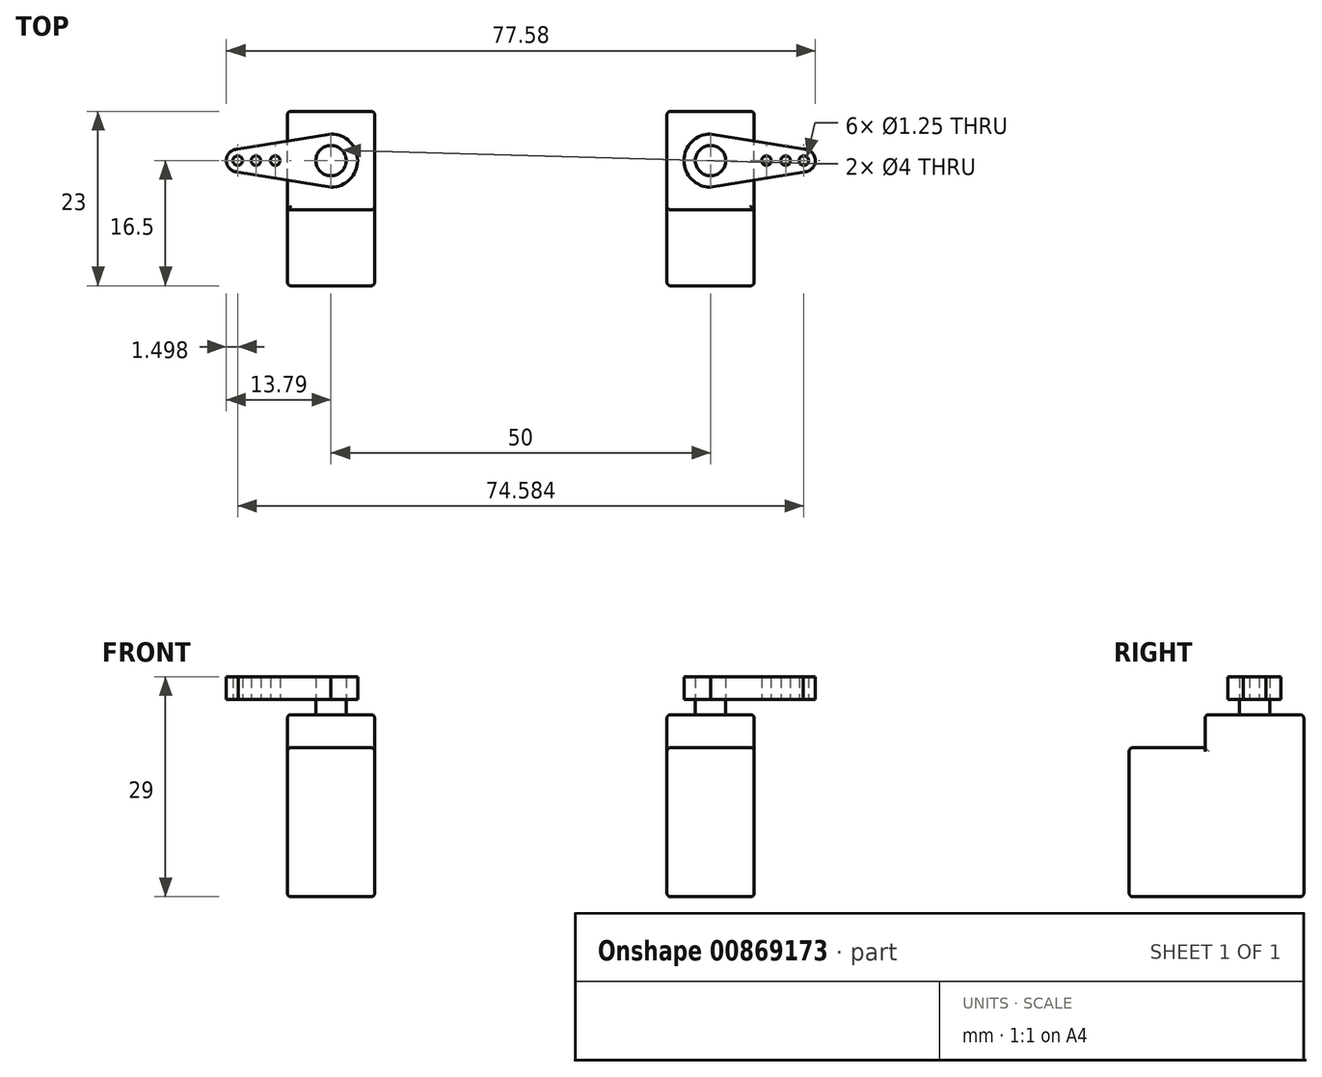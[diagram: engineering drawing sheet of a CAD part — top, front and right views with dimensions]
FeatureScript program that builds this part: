
annotation { "Feature Type Name" : "Feature", "Feature Type Description" : "" }
export const myFeature = defineFeature(function(context is Context, id is Id, definition is map)
    precondition{}
    {
        {
            var Q0;
            Q0=qCreatedBy(makeId("Top.planeOp"),FACE);
            var sketch = newSketch(context, id + "F0", { "sketchPlane" : qUnion([Q0])});
            skLineSegment(sketch, "E0.bottom", {"start": v(5.75, -11.5) * mm, "end": v(-5.75, -11.5) * mm});
            skLineSegment(sketch, "E0.top", {"start": v(5.75, 11.5) * mm, "end": v(-5.75, 11.5) * mm});
            skLineSegment(sketch, "E0.left", {"start": v(5.75, -11.5) * mm, "end": v(5.75, 11.5) * mm});
            skLineSegment(sketch, "E0.right", {"start": v(-5.75, -11.5) * mm, "end": v(-5.75, 11.5) * mm});
            skPoint(sketch, "E0.middle", {"position": v(0, 0) * mm});
            skSolve(sketch);
        }
        {
            var Q0;
            Q0 = qSketchRegion(id + "F0", true);
            extrude(context, id + "F1", {"entities" : qUnion([Q0]), "depth" : 19.65 * mm, "offsetDistance" : 25 * mm});
        }
        {
            var Q0;
            Q0=makeQuery(id+"F1.opExtrude","CAP_FACE",FACE,{"disambiguationData":[OSD([sQuery(id+"F0.wireOp",EDGE,"E0.bottom"),sQuery(id+"F0.wireOp",EDGE,"E0.top"),sQuery(id+"F0.wireOp",EDGE,"E0.left"),sQuery(id+"F0.wireOp",EDGE,"E0.right")])],"isStart":false});
            var sketch = newSketch(context, id + "F2", { "sketchPlane" : qUnion([Q0])});
            skLineSegment(sketch, "E1.bottom", {"start": v(-5.75, 11.5) * mm, "end": v(5.75, 11.5) * mm});
            skLineSegment(sketch, "E1.top", {"start": v(-5.75, -1.5) * mm, "end": v(5.75, -1.5) * mm});
            skLineSegment(sketch, "E1.left", {"start": v(-5.75, 11.5) * mm, "end": v(-5.75, -1.5) * mm});
            skLineSegment(sketch, "E1.right", {"start": v(5.75, 11.5) * mm, "end": v(5.75, -1.5) * mm});
            skSolve(sketch);
        }
        {
            var Q0;
            Q0=makeQuery(id+"F2.imprint","IMPRINT",FACE,{"disambiguationData":[TD([[makeQuery(id+"F2.imprint","IMPRINT",EDGE,{"derivedFrom":sQuery(id+"F2.wireOp",EDGE,"E1.bottom")}),1.0]])]});
            extrude(context, id + "F3", {"entities" : qUnion([Q0]), "operationType" : NewBodyOperationType.ADD, "depth" : 4.35 * mm, "offsetDistance" : 25 * mm});
        }
        {
            var Q0;
            Q0=makeQuery(id+"F1.opExtrude","SWEPT_EDGE",EDGE,{"disambiguationData":[OSD([sQuery(id+"F0.wireOp",EDGE,"E0.bottom"),sQuery(id+"F0.wireOp",EDGE,"E0.right")])]});
            var Q1;
            Q1=makeQuery(id+"F1.opExtrude","SWEPT_EDGE",EDGE,{"disambiguationData":[OSD([sQuery(id+"F0.wireOp",EDGE,"E0.bottom"),sQuery(id+"F0.wireOp",EDGE,"E0.left")])]});
            var Q2;
            Q2=makeQuery(id+"F3.boolean.opBoolean","MERGE",EDGE,{"derivedFrom":[makeQuery(id+"F1.opExtrude","SWEPT_EDGE",EDGE,{"disambiguationData":[OSD([sQuery(id+"F0.wireOp",EDGE,"E0.top"),sQuery(id+"F0.wireOp",EDGE,"E0.right")])]}),makeQuery(id+"F3.opExtrude","SWEPT_EDGE",EDGE,{"disambiguationData":[OSD([sQuery(id+"F2.wireOp",EDGE,"E1.bottom"),sQuery(id+"F2.wireOp",EDGE,"E1.left")])]})]});
            var Q3;
            Q3=makeQuery(id+"F3.boolean.opBoolean","MERGE",EDGE,{"derivedFrom":[makeQuery(id+"F1.opExtrude","SWEPT_EDGE",EDGE,{"disambiguationData":[OSD([sQuery(id+"F0.wireOp",EDGE,"E0.top"),sQuery(id+"F0.wireOp",EDGE,"E0.left")])]}),makeQuery(id+"F3.opExtrude","SWEPT_EDGE",EDGE,{"disambiguationData":[OSD([sQuery(id+"F2.wireOp",EDGE,"E1.bottom"),sQuery(id+"F2.wireOp",EDGE,"E1.right")])]})]});
            var Q4;
            Q4=makeQuery(id+"F1.opExtrude","CAP_EDGE",EDGE,{"disambiguationData":[OSD([sQuery(id+"F0.wireOp",EDGE,"E0.left")])],"isStart":true});
            var Q5;
            Q5=makeQuery(id+"F1.opExtrude","CAP_EDGE",EDGE,{"disambiguationData":[OSD([sQuery(id+"F0.wireOp",EDGE,"E0.right")])],"isStart":true});
            var Q6;
            Q6=makeQuery(id+"F1.opExtrude","CAP_EDGE",EDGE,{"disambiguationData":[OSD([sQuery(id+"F0.wireOp",EDGE,"E0.bottom")])],"isStart":false});
            var Q7;
            Q7=makeQuery(id+"F1.opExtrude","CAP_EDGE",EDGE,{"disambiguationData":[OSD([sQuery(id+"F0.wireOp",EDGE,"E0.right")])],"isStart":false});
            var Q8;
            Q8=makeQuery(id+"F3.opExtrude","SWEPT_EDGE",EDGE,{"disambiguationData":[OSD([sQuery(id+"F0.wireOp",EDGE,"E0.right"),sQuery(id+"F2.wireOp",EDGE,"E1.top"),sQuery(id+"F2.wireOp",EDGE,"E1.left")])]});
            var Q9;
            Q9=makeQuery(id+"F3.opExtrude","CAP_EDGE",EDGE,{"disambiguationData":[OSD([sQuery(id+"F2.wireOp",EDGE,"E1.left")])],"isStart":false});
            var Q10;
            Q10=makeQuery(id+"F3.opExtrude","CAP_EDGE",EDGE,{"disambiguationData":[OSD([sQuery(id+"F2.wireOp",EDGE,"E1.top")])],"isStart":false});
            var Q11;
            Q11=makeQuery(id+"F3.opExtrude","CAP_EDGE",EDGE,{"disambiguationData":[OSD([sQuery(id+"F2.wireOp",EDGE,"E1.right")])],"isStart":false});
            var Q12;
            Q12=makeQuery(id+"F1.opExtrude","CAP_EDGE",EDGE,{"disambiguationData":[OSD([sQuery(id+"F0.wireOp",EDGE,"E0.left")])],"isStart":false});
            var Q13;
            Q13=makeQuery(id+"F3.opExtrude","CAP_EDGE",EDGE,{"disambiguationData":[OSD([sQuery(id+"F2.wireOp",EDGE,"E1.bottom")])],"isStart":false});
            var Q14;
            Q14=makeQuery(id+"F1.opExtrude","CAP_EDGE",EDGE,{"disambiguationData":[OSD([sQuery(id+"F0.wireOp",EDGE,"E0.top")])],"isStart":true});
            var Q15;
            Q15=makeQuery(id+"F1.opExtrude","CAP_EDGE",EDGE,{"disambiguationData":[OSD([sQuery(id+"F0.wireOp",EDGE,"E0.bottom")])],"isStart":true});
            fillet(context, id + "F4", {"entities" : qUnion([Q0, Q1, Q2, Q3, Q4, Q5, Q6, Q7, Q8, Q9, Q10, Q11, Q12, Q13, Q14, Q15]), "radius" : .5 * mm, "tangentPropagation" : true, "allowEdgeOverflow" : false});
        }
        {
            var Q0;
            Q0=makeQuery(id+"F3.opExtrude","CAP_FACE",FACE,{"disambiguationData":[OSD([sQuery(id+"F2.wireOp",EDGE,"E1.bottom"),sQuery(id+"F2.wireOp",EDGE,"E1.top"),sQuery(id+"F2.wireOp",EDGE,"E1.left"),sQuery(id+"F2.wireOp",EDGE,"E1.right")])],"isStart":false});
            var sketch = newSketch(context, id + "F5", { "sketchPlane" : qUnion([Q0])});
            skCircle(sketch, "E2", {"center": v(0, 5) * mm, "radius": 2 * mm});
            skSolve(sketch);
        }
        {
            var Q0;
            Q0=makeQuery(id+"F5.imprint","IMPRINT",FACE,{"disambiguationData":[TD([[makeQuery(id+"F5.imprint","IMPRINT",EDGE,{"derivedFrom":sQuery(id+"F5.wireOp",EDGE,"E2")}),1.0]])]});
            extrude(context, id + "F6", {"entities" : qUnion([Q0]), "operationType" : NewBodyOperationType.ADD, "depth" : 5 * mm, "offsetDistance" : 25 * mm});
        }
        {
            var Q0;
            Q0=makeQuery(id+"F3.opExtrude","CAP_FACE",FACE,{"disambiguationData":[OSD([sQuery(id+"F2.wireOp",EDGE,"E1.bottom"),sQuery(id+"F2.wireOp",EDGE,"E1.top"),sQuery(id+"F2.wireOp",EDGE,"E1.left"),sQuery(id+"F2.wireOp",EDGE,"E1.right")])],"isStart":false});
            var sketch = newSketch(context, id + "F7", { "sketchPlane" : qUnion([Q0])});
            skCircle(sketch, "E3.0", {"center": v(0, 5) * mm, "radius": 2 * mm});
            skArc(sketch, "E4", {"start": v(0, 8.5) * mm, "mid": v(-3.5, 5) * mm, "end": v(0, 1.5) * mm});
            skArc(sketch, "E5", {"start": v(12.2, 3.5) * mm, "mid": v(13.8, 4.97) * mm, "end": v(12.26, 6.5) * mm});
            skLineSegment(sketch, "E6", {"start": v(0, 8.5) * mm, "end": v(12.26, 6.5) * mm});
            skLineSegment(sketch, "E7", {"start": v(0, 1.5) * mm, "end": v(12.2, 3.5) * mm});
            skCircle(sketch, "E8", {"center": v(12.3, 5) * mm, "radius": 0.62 * mm});
            skCircle(sketch, "E9", {"center": v(9.89, 5) * mm, "radius": 0.62 * mm});
            skCircle(sketch, "E10", {"center": v(7.35, 5) * mm, "radius": 0.62 * mm});
            skSolve(sketch);
        }
        {
            var Q0;
            Q0=makeQuery(id+"F7.imprint","IMPRINT",FACE,{"disambiguationData":[TD([[makeQuery(id+"F7.imprint","IMPRINT",EDGE,{"derivedFrom":sQuery(id+"F7.wireOp",EDGE,"E3.0")}),-1.0]])]});
            var Q1;
            {var subQ1=sQuery(id+"F7.wireOp",EDGE,"E5");Q1=makeQuery(id+"F7.imprint","IMPRINT",FACE,{"disambiguationData":[TD([[makeQuery(id+"F7.imprint","IMPRINT",EDGE,{"derivedFrom":subQ1}),1.0]])]});}
            extrude(context, id + "F8", {"entities" : qUnion([Q0, Q1]), "depth" : 3 * mm, "offsetDistance" : 25 * mm});
        }
        {
            var Q0;
            Q0=makeQuery(id+"F8.opExtrude","SWEPT_BODY",BODY,{"disambiguationData":[OSD([sQuery(id+"F7.wireOp",EDGE,"E3.0"),sQuery(id+"F7.wireOp",EDGE,"E4"),sQuery(id+"F7.wireOp",EDGE,"E5"),sQuery(id+"F7.wireOp",EDGE,"E6"),sQuery(id+"F7.wireOp",EDGE,"E7"),sQuery(id+"F7.wireOp",EDGE,"E8"),sQuery(id+"F7.wireOp",EDGE,"E9"),sQuery(id+"F7.wireOp",EDGE,"E10")])]});
            transform(context, id + "F9", {"entities" : qUnion([Q0]), "transformType" : TransformType.TRANSLATION_3D, "dx" : 0 * mm, "dy" : 0 * mm, "dz" : 2 * mm, "makeCopy" : false});
        }
        {
            var Q0;
            Q0=makeQuery(id+"F1.opExtrude","SWEPT_BODY",BODY,{"disambiguationData":[OSD([sQuery(id+"F0.wireOp",EDGE,"E0.bottom"),sQuery(id+"F0.wireOp",EDGE,"E0.top"),sQuery(id+"F0.wireOp",EDGE,"E0.left"),sQuery(id+"F0.wireOp",EDGE,"E0.right")])]});
            var Q1;
            Q1=makeQuery(id+"F8.opExtrude","SWEPT_BODY",BODY,{"disambiguationData":[OSD([sQuery(id+"F7.wireOp",EDGE,"E3.0"),sQuery(id+"F7.wireOp",EDGE,"E4"),sQuery(id+"F7.wireOp",EDGE,"E5"),sQuery(id+"F7.wireOp",EDGE,"E6"),sQuery(id+"F7.wireOp",EDGE,"E7"),sQuery(id+"F7.wireOp",EDGE,"E8"),sQuery(id+"F7.wireOp",EDGE,"E9"),sQuery(id+"F7.wireOp",EDGE,"E10")])]});
            var Q2;
            Q2=qCreatedBy(makeId("Right.planeOp"),FACE);
            mirror(context, id + "F10", {"entities" : qUnion([Q0, Q1]), "mirrorPlane" : qUnion([Q2])});
        }
        {
            var Q0;
            Q0=makeQuery(id+"F10.opPattern","COPY",BODY,{"derivedFrom":makeQuery(id+"F1.opExtrude","SWEPT_BODY",BODY,{"disambiguationData":[OSD([sQuery(id+"F0.wireOp",EDGE,"E0.bottom"),sQuery(id+"F0.wireOp",EDGE,"E0.top"),sQuery(id+"F0.wireOp",EDGE,"E0.left"),sQuery(id+"F0.wireOp",EDGE,"E0.right")])]}),"instanceName":"1"});
            var Q1;
            Q1=makeQuery(id+"F10.opPattern","COPY",BODY,{"derivedFrom":makeQuery(id+"F8.opExtrude","SWEPT_BODY",BODY,{"disambiguationData":[OSD([sQuery(id+"F7.wireOp",EDGE,"E3.0"),sQuery(id+"F7.wireOp",EDGE,"E4"),sQuery(id+"F7.wireOp",EDGE,"E5"),sQuery(id+"F7.wireOp",EDGE,"E6"),sQuery(id+"F7.wireOp",EDGE,"E7"),sQuery(id+"F7.wireOp",EDGE,"E8"),sQuery(id+"F7.wireOp",EDGE,"E9"),sQuery(id+"F7.wireOp",EDGE,"E10")])]}),"instanceName":"1"});
            transform(context, id + "F11", {"entities" : qUnion([Q0, Q1]), "transformType" : TransformType.TRANSLATION_3D, "dx" : -50 * mm, "dy" : 0 * mm, "dz" : 0 * mm, "makeCopy" : false});
        }
    });
